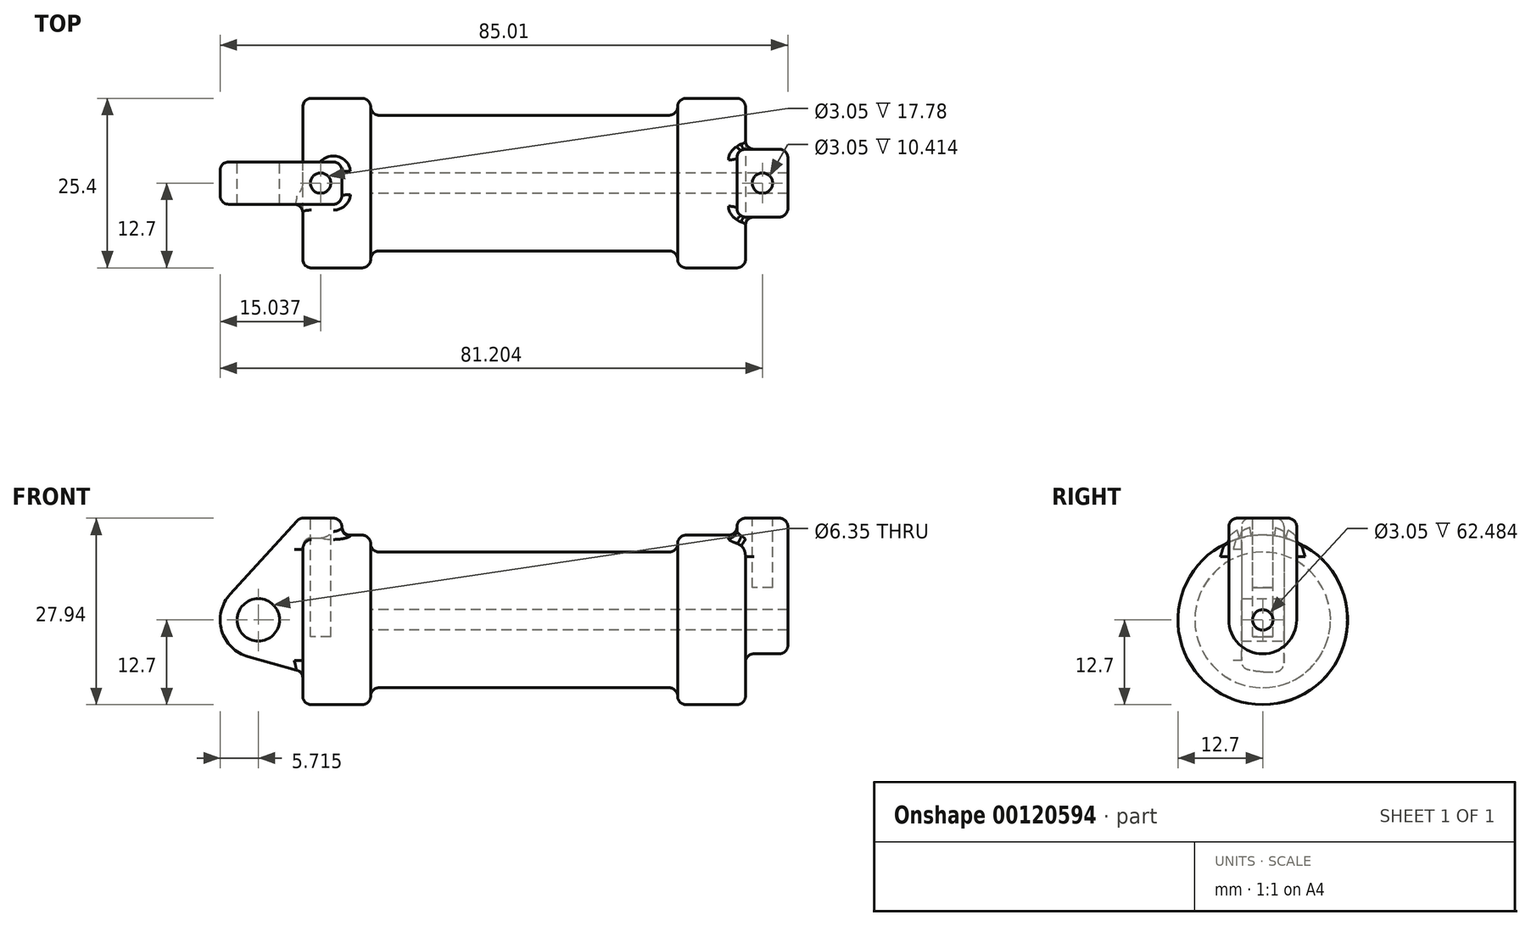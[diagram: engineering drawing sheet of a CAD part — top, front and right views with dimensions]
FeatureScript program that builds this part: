
annotation { "Feature Type Name" : "Feature", "Feature Type Description" : "" }
export const myFeature = defineFeature(function(context is Context, id is Id, definition is map)
    precondition{}
    {
        {
            var Q0;
            Q0=qCreatedBy(makeId("Front.planeOp"),FACE);
            var sketch = newSketch(context, id + "F0", { "sketchPlane" : qUnion([Q0])});
            skLineSegment(sketch, "E0", {"start": v(0, 0) * mm, "end": v(0, 12.7) * mm});
            skLineSegment(sketch, "E1", {"start": v(0, 12.7) * mm, "end": v(10.16, 12.7) * mm});
            skLineSegment(sketch, "E2", {"start": v(10.16, 12.7) * mm, "end": v(10.16, 10.16) * mm});
            skLineSegment(sketch, "E3", {"start": v(10.16, 10.16) * mm, "end": v(56.13, 10.16) * mm});
            skLineSegment(sketch, "E4", {"start": v(56.13, 10.16) * mm, "end": v(56.13, 12.7) * mm});
            skLineSegment(sketch, "E5", {"start": v(56.13, 12.7) * mm, "end": v(66.3, 12.7) * mm});
            skLineSegment(sketch, "E6", {"start": v(66.3, 12.7) * mm, "end": v(66.3, 0) * mm});
            skLineSegment(sketch, "E7", {"start": v(66.3, 0) * mm, "end": v(0, 0) * mm});
            skLineSegment(sketch, "E8", {"start": v(5.84, 15.24) * mm, "end": v(-0.5, 15.24) * mm});
            skLineSegment(sketch, "E9", {"start": v(-0.5, 15.24) * mm, "end": v(-10.88, 3.85) * mm});
            skLineSegment(sketch, "E10", {"start": v(0, 0) * mm, "end": v(-6.65, 0) * mm});
            skCircle(sketch, "E11", {"center": v(-6.65, 0) * mm, "radius": 5.72 * mm});
            skCircle(sketch, "E12", {"center": v(-6.65, 0) * mm, "radius": 3.18 * mm});
            skLineSegment(sketch, "E13", {"start": v(5.84, 15.24) * mm, "end": v(5.84, -9.4) * mm});
            skLineSegment(sketch, "E14", {"start": v(5.84, -9.4) * mm, "end": v(-8.18, -5.5) * mm});
            skSolve(sketch);
        }
        {
            var Q0;
            {var subQ0=sQuery(id+"F0.wireOp",EDGE,"E2");Q0=makeQuery(id+"F0.imprint","IMPRINT",FACE,{"disambiguationData":[TD([[makeQuery(id+"F0.imprint","IMPRINT",EDGE,{"derivedFrom":subQ0}),-1.0]])]});}
            var Q1;
            {var subQ0=sQuery(id+"F0.wireOp",EDGE,"E0");Q1=makeQuery(id+"F0.imprint","IMPRINT",FACE,{"disambiguationData":[TD([[makeQuery(id+"F0.imprint","IMPRINT",EDGE,{"derivedFrom":subQ0}),-1.0]])]});}
            var Q2;
            Q2=sQuery(id+"F0.wireOp",EDGE,"E7");
            revolve(context, id + "F1", {"entities" : qUnion([Q0, Q1]), "axis" : qUnion([Q2]), "revolveType" : RevolveType.FULL});
        }
        {
            var Q0;
            {var subQ4=sQuery(id+"F0.wireOp",EDGE,"E12");Q0=makeQuery(id+"F0.imprint","IMPRINT",FACE,{"disambiguationData":[TD([[makeQuery(id+"F0.imprint","IMPRINT",EDGE,{"derivedFrom":subQ4}),-1.0]])]});}
            var Q1;
            {var subQ3=sQuery(id+"F0.wireOp",EDGE,"E0");Q1=makeQuery(id+"F0.imprint","IMPRINT",FACE,{"disambiguationData":[TD([[makeQuery(id+"F0.imprint","IMPRINT",EDGE,{"derivedFrom":subQ3}),1.0]])]});}
            var Q2;
            {var subQ0=sQuery(id+"F0.wireOp",EDGE,"E14");Q2=makeQuery(id+"F0.imprint","IMPRINT",FACE,{"disambiguationData":[TD([[makeQuery(id+"F0.imprint","IMPRINT",EDGE,{"derivedFrom":subQ0}),-1.0]])]});}
            var Q3;
            {var subQ0=sQuery(id+"F0.wireOp",EDGE,"E0");Q3=makeQuery(id+"F0.imprint","IMPRINT",FACE,{"disambiguationData":[TD([[makeQuery(id+"F0.imprint","IMPRINT",EDGE,{"derivedFrom":subQ0}),-1.0]])]});}
            extrude(context, id + "F2", {"entities" : qUnion([Q0, Q1, Q2, Q3]), "operationType" : NewBodyOperationType.ADD, "endBound" : BoundingType.SYMMETRIC, "depth" : 6.35 * mm});
        }
        {
            var Q0;
            Q0=makeQuery(id+"F1.opRevolve","SWEPT_FACE",FACE,{"disambiguationData":[OSD([sQuery(id+"F0.wireOp",EDGE,"E6")])]});
            var sketch = newSketch(context, id + "F3", { "sketchPlane" : qUnion([Q0])});
            skCircle(sketch, "E15", {"center": v(0, 0) * mm, "radius": 1.52 * mm});
            skCircle(sketch, "E16", {"center": v(0, 0) * mm, "radius": 5.08 * mm});
            skLineSegment(sketch, "E17", {"start": v(5.08, 0) * mm, "end": v(5.08, 15.24) * mm});
            skLineSegment(sketch, "E18", {"start": v(-5.08, 0) * mm, "end": v(-5.08, 15.24) * mm});
            skLineSegment(sketch, "E19", {"start": v(-5.08, 15.24) * mm, "end": v(5.08, 15.24) * mm});
            skSolve(sketch);
        }
        {
            var Q0;
            Q0 = qSketchRegion(id + "F3", true);
            extrude(context, id + "F4", {"entities" : qUnion([Q0]), "operationType" : NewBodyOperationType.ADD, "depth" : 6.35 * mm, "hasSecondDirection" : true, "secondDirectionOppositeDirection" : true, "secondDirectionDepth" : 1.27 * mm});
        }
        {
            var Q0;
            Q0=makeQuery(id+"F3.imprint","IMPRINT",FACE,{"disambiguationData":[TD([[makeQuery(id+"F3.imprint","IMPRINT",EDGE,{"derivedFrom":sQuery(id+"F3.wireOp",EDGE,"E15")}),1.0]])]});
            var Q1;
            Q1=makeQuery(id+"F1.opRevolve","SWEPT_FACE",FACE,{"disambiguationData":[OSD([sQuery(id+"F0.wireOp",EDGE,"E2")])]});
            extrude(context, id + "F5", {"entities" : qUnion([Q0]), "operationType" : NewBodyOperationType.REMOVE, "endBound" : BoundingType.UP_TO_SURFACE, "oppositeDirection" : true, "endBoundEntityFace" : qUnion([Q1]), "depth" : 25.4 * mm});
        }
        {
            var Q0;
            Q0=makeQuery(id+"F4.opExtrude","SWEPT_FACE",FACE,{"disambiguationData":[OSD([sQuery(id+"F3.wireOp",EDGE,"E19")])]});
            var sketch = newSketch(context, id + "F6", { "sketchPlane" : qUnion([Q0])});
            skLineSegment(sketch, "E20.0", {"start": v(5.84, 3.18) * mm, "end": v(-0.5, 3.18) * mm, "construction": true});
            skLineSegment(sketch, "E21.0", {"start": v(-0.5, -3.18) * mm, "end": v(-0.5, 3.17) * mm, "construction": true});
            skLineSegment(sketch, "E22.0", {"start": v(72.64, 5.08) * mm, "end": v(65.02, 5.08) * mm, "construction": true});
            skLineSegment(sketch, "E23.0", {"start": v(72.64, -5.08) * mm, "end": v(72.64, 5.08) * mm, "construction": true});
            skCircle(sketch, "E24", {"center": v(2.67, 0) * mm, "radius": 1.52 * mm});
            skPoint(sketch, "E24.centerSnap0", {"position": v(2.67, 3.18) * mm});
            skPoint(sketch, "E24.centerSnap1", {"position": v(-0.5, 0) * mm});
            skCircle(sketch, "E25", {"center": v(68.83, 0) * mm, "radius": 1.52 * mm});
            skPoint(sketch, "E25.centerSnap0", {"position": v(72.64, 0) * mm});
            skPoint(sketch, "E25.centerSnap1", {"position": v(68.83, 5.08) * mm});
            skSolve(sketch);
        }
        {
            var Q0;
            Q0=makeQuery(id+"F6.imprint","IMPRINT",FACE,{"disambiguationData":[TD([[makeQuery(id+"F6.imprint","IMPRINT",EDGE,{"derivedFrom":sQuery(id+"F6.wireOp",EDGE,"E24")}),1.0]])]});
            extrude(context, id + "F7", {"entities" : qUnion([Q0]), "operationType" : NewBodyOperationType.REMOVE, "oppositeDirection" : true, "depth" : 17.78 * mm});
        }
        {
            var Q0;
            Q0=makeQuery(id+"F6.imprint","IMPRINT",FACE,{"disambiguationData":[TD([[makeQuery(id+"F6.imprint","IMPRINT",EDGE,{"derivedFrom":sQuery(id+"F6.wireOp",EDGE,"E25")}),1.0]])]});
            extrude(context, id + "F8", {"entities" : qUnion([Q0]), "operationType" : NewBodyOperationType.REMOVE, "oppositeDirection" : true, "depth" : 10.4 * mm});
        }
        {
            var Q0;
            Q0=makeQuery(id+"F1.opRevolve","SWEPT_EDGE",EDGE,{"disambiguationData":[OSD([sQuery(id+"F0.wireOp",EDGE,"E0"),sQuery(id+"F0.wireOp",EDGE,"E1")])]});
            var Q1;
            Q1=makeQuery(id+"F1.opRevolve","SWEPT_EDGE",EDGE,{"disambiguationData":[OSD([sQuery(id+"F0.wireOp",EDGE,"E1"),sQuery(id+"F0.wireOp",EDGE,"E2")])]});
            var Q2;
            Q2=makeQuery(id+"F1.opRevolve","SWEPT_EDGE",EDGE,{"disambiguationData":[OSD([sQuery(id+"F0.wireOp",EDGE,"E2"),sQuery(id+"F0.wireOp",EDGE,"E3")])]});
            var Q3;
            Q3=makeQuery(id+"F1.opRevolve","SWEPT_EDGE",EDGE,{"disambiguationData":[OSD([sQuery(id+"F0.wireOp",EDGE,"E4"),sQuery(id+"F0.wireOp",EDGE,"E5")])]});
            var Q4;
            Q4=makeQuery(id+"F1.opRevolve","SWEPT_EDGE",EDGE,{"disambiguationData":[OSD([sQuery(id+"F0.wireOp",EDGE,"E5"),sQuery(id+"F0.wireOp",EDGE,"E6")])]});
            var Q5;
            Q5=makeQuery(id+"F1.opRevolve","SWEPT_EDGE",EDGE,{"disambiguationData":[OSD([sQuery(id+"F0.wireOp",EDGE,"E3"),sQuery(id+"F0.wireOp",EDGE,"E4")])]});
            fillet(context, id + "F9", {"entities" : qUnion([Q0, Q1, Q2, Q3, Q4, Q5]), "radius" : 1.27 * mm, "tangentPropagation" : true, "allowEdgeOverflow" : false});
        }
        {
            var Q0;
            Q0=makeQuery(id+"F2.opExtrude","CAP_EDGE",EDGE,{"disambiguationData":[OSD([sQuery(id+"F0.wireOp",EDGE,"E14")])],"isStart":false});
            var Q1;
            Q1=makeQuery(id+"F2.opExtrude","SWEPT_EDGE",EDGE,{"disambiguationData":[OSD([sQuery(id+"F0.wireOp",EDGE,"E8"),sQuery(id+"F0.wireOp",EDGE,"E9")])]});
            var Q2;
            Q2=makeQuery(id+"F2.opExtrude","CAP_EDGE",EDGE,{"disambiguationData":[OSD([sQuery(id+"F0.wireOp",EDGE,"E8")])],"isStart":false});
            var Q3;
            Q3=makeQuery(id+"F2.opExtrude","CAP_EDGE",EDGE,{"disambiguationData":[OSD([sQuery(id+"F0.wireOp",EDGE,"E8")])],"isStart":true});
            var Q4;
            Q4=makeQuery(id+"F2.opExtrude","CAP_EDGE",EDGE,{"disambiguationData":[OSD([sQuery(id+"F0.wireOp",EDGE,"E9")])],"isStart":true});
            var Q5;
            Q5=makeQuery(id+"F2.boolean.opBoolean","INTERSECT",EDGE,{"derivedFrom":[makeQuery(id+"F1.opRevolve","SWEPT_FACE",FACE,{"disambiguationData":[OSD([sQuery(id+"F0.wireOp",EDGE,"E0")])]}),makeQuery(id+"F2.opExtrude","CAP_FACE",FACE,{"disambiguationData":[OSD([sQuery(id+"F0.wireOp",EDGE,"E8"),sQuery(id+"F0.wireOp",EDGE,"E9"),sQuery(id+"F0.wireOp",EDGE,"E11"),sQuery(id+"F0.wireOp",EDGE,"E12"),sQuery(id+"F0.wireOp",EDGE,"E13"),sQuery(id+"F0.wireOp",EDGE,"E14")])],"isStart":false})]});
            var Q6;
            Q6=makeQuery(id+"F2.boolean.opBoolean","INTERSECT",EDGE,{"derivedFrom":[makeQuery(id+"F1.opRevolve","SWEPT_FACE",FACE,{"disambiguationData":[OSD([sQuery(id+"F0.wireOp",EDGE,"E1")])]}),makeQuery(id+"F2.opExtrude","SWEPT_FACE",FACE,{"disambiguationData":[OSD([sQuery(id+"F0.wireOp",EDGE,"E13")])]})]});
            var Q7;
            Q7=makeQuery(id+"F2.opExtrude","CAP_EDGE",EDGE,{"disambiguationData":[OSD([sQuery(id+"F0.wireOp",EDGE,"E13")])],"isStart":false});
            var Q8;
            Q8=makeQuery(id+"F2.opExtrude","CAP_EDGE",EDGE,{"disambiguationData":[OSD([sQuery(id+"F0.wireOp",EDGE,"E13")])],"isStart":true});
            var Q9;
            Q9=makeQuery(id+"F2.opExtrude","SWEPT_EDGE",EDGE,{"disambiguationData":[OSD([sQuery(id+"F0.wireOp",EDGE,"E8"),sQuery(id+"F0.wireOp",EDGE,"E13")])]});
            fillet(context, id + "F10", {"entities" : qUnion([Q0, Q1, Q2, Q3, Q4, Q5, Q6, Q7, Q8, Q9]), "radius" : 1.27 * mm, "tangentPropagation" : true, "allowEdgeOverflow" : false});
        }
        {
            var Q0;
            Q0=makeQuery(id+"F4.opExtrude","CAP_FACE",FACE,{"disambiguationData":[OSD([sQuery(id+"F3.wireOp",EDGE,"E15"),sQuery(id+"F3.wireOp",EDGE,"E16"),sQuery(id+"F3.wireOp",EDGE,"E17"),sQuery(id+"F3.wireOp",EDGE,"E18"),sQuery(id+"F3.wireOp",EDGE,"E19")])],"isStart":true});
            var Q1;
            Q1=makeQuery(id+"F4.opExtrude","SWEPT_FACE",FACE,{"disambiguationData":[OSD([sQuery(id+"F3.wireOp",EDGE,"E18")])]});
            var Q2;
            Q2=makeQuery(id+"F4.opExtrude","CAP_EDGE",EDGE,{"disambiguationData":[OSD([sQuery(id+"F3.wireOp",EDGE,"E19")])],"isStart":false});
            var Q3;
            Q3=makeQuery(id+"F4.opExtrude","SWEPT_EDGE",EDGE,{"disambiguationData":[OSD([sQuery(id+"F3.wireOp",EDGE,"E17"),sQuery(id+"F3.wireOp",EDGE,"E19")])]});
            fillet(context, id + "F11", {"entities" : qUnion([Q0, Q1, Q2, Q3]), "radius" : 1.27 * mm, "tangentPropagation" : true, "allowEdgeOverflow" : false});
        }
    });
